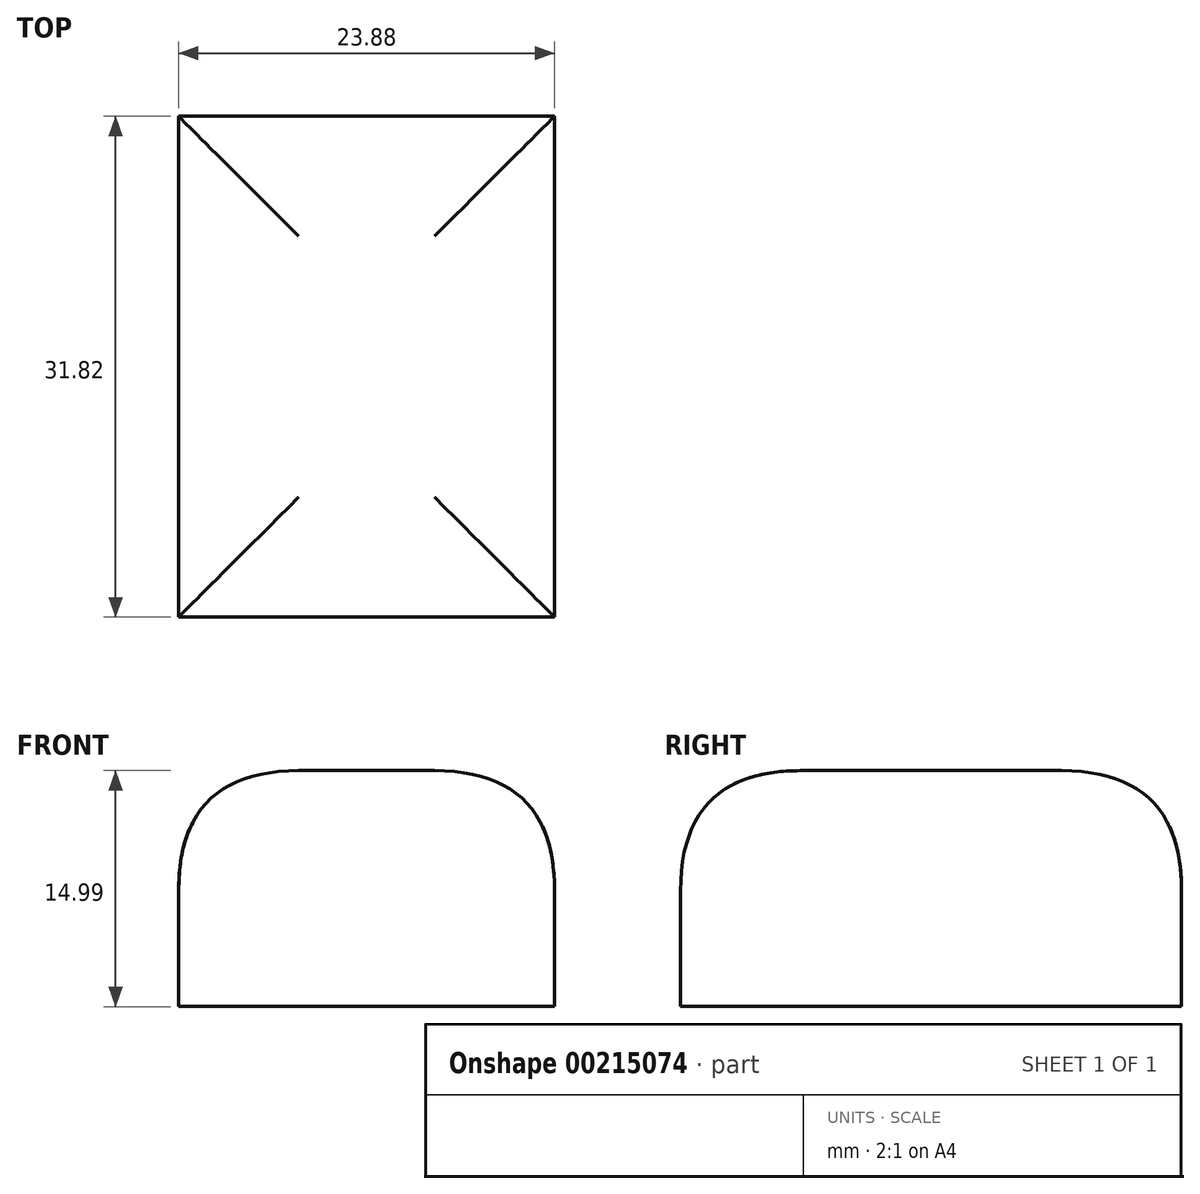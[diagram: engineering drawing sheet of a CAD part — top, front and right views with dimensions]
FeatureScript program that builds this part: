
annotation { "Feature Type Name" : "Feature", "Feature Type Description" : "" }
export const myFeature = defineFeature(function(context is Context, id is Id, definition is map)
    precondition{}
    {
        {
            var Q0;
            Q0=qCreatedBy(makeId("Top.planeOp"),FACE);
            var sketch = newSketch(context, id + "F0", { "sketchPlane" : qUnion([Q0])});
            skLineSegment(sketch, "E0.bottom", {"start": v(0, 0) * mm, "end": v(0, 0) * mm});
            skLineSegment(sketch, "E0.top", {"start": v(0, 0) * mm, "end": v(0, 0) * mm});
            skLineSegment(sketch, "E0.left", {"start": v(0, 0) * mm, "end": v(0, 0) * mm});
            skLineSegment(sketch, "E0.right", {"start": v(0, 0) * mm, "end": v(0, 0) * mm});
            skLineSegment(sketch, "E1.bottom", {"start": v(23.88, 0) * mm, "end": v(0, 0) * mm});
            skLineSegment(sketch, "E1.top", {"start": v(23.88, -31.82) * mm, "end": v(0, -31.82) * mm});
            skLineSegment(sketch, "E1.left", {"start": v(23.88, 0) * mm, "end": v(23.88, -31.82) * mm});
            skLineSegment(sketch, "E1.right", {"start": v(0, 0) * mm, "end": v(0, -31.82) * mm});
            skSolve(sketch);
        }
        {
            var Q0;
            Q0 = qSketchRegion(id + "F0", true);
            extrude(context, id + "F3", {"entities" : qUnion([Q0]), "depth" : 12.7 * mm});
        }
        {
            var Q0;
            Q0=makeQuery(id+"F3.opExtrude","CAP_EDGE",EDGE,{"disambiguationData":[OSD([sQuery(id+"F0.wireOp",EDGE,"E1.left")])],"isStart":false});
            var Q1;
            Q1=makeQuery(id+"F3.opExtrude","CAP_EDGE",EDGE,{"disambiguationData":[OSD([sQuery(id+"F0.wireOp",EDGE,"E1.right")])],"isStart":false});
            var Q2;
            Q2=makeQuery(id+"F3.opExtrude","CAP_EDGE",EDGE,{"disambiguationData":[OSD([sQuery(id+"F0.wireOp",EDGE,"E1.bottom")])],"isStart":false});
            var Q3;
            Q3=makeQuery(id+"F3.opExtrude","CAP_EDGE",EDGE,{"disambiguationData":[OSD([sQuery(id+"F0.wireOp",EDGE,"E1.top")])],"isStart":false});
            fillet(context, id + "F1", {"entities" : qUnion([Q0, Q1, Q2, Q3]), "radius" : 7.62 * mm, "tangentPropagation" : true, "rho" : 0.5, "crossSection" : FilletCrossSection.CONIC, "allowEdgeOverflow" : false});
        }
        {
            var Q0;
            Q0=makeQuery(id+"F3.opExtrude","CAP_FACE",FACE,{"disambiguationData":[OSD([sQuery(id+"F0.wireOp",EDGE,"E1.bottom"),sQuery(id+"F0.wireOp",EDGE,"E1.top"),sQuery(id+"F0.wireOp",EDGE,"E1.left"),sQuery(id+"F0.wireOp",EDGE,"E1.right")])],"isStart":true});
            extrude(context, id + "F2", {"entities" : qUnion([Q0]), "operationType" : NewBodyOperationType.ADD, "depth" : 2.3 * mm});
        }
    });
